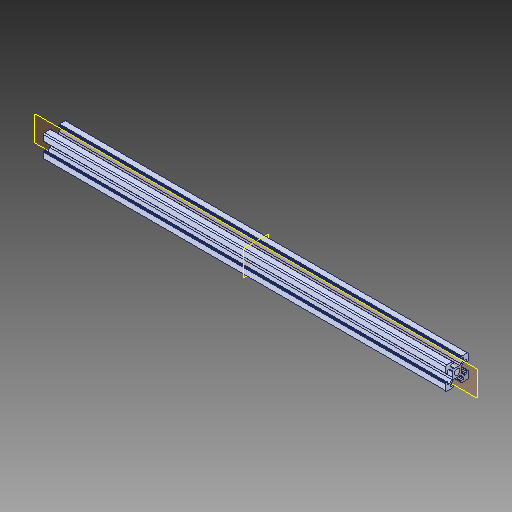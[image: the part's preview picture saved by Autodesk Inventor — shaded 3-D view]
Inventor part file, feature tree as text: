
AUTODESK INVENTOR PART (.ipt)
format: ipt  version: 2018 (Build 220112000, 112)  size: 377,344 bytes
history: native  units: in
note: dims shown in document units (in); Inventor stores cm internally (conversion verified against a paired STEP export)
features: extrude x1, plane x1, sketch x1, projected_geometry x1, fillet x1
ambient origin geometry x8: Origin, YZ Plane, XZ Plane, XY Plane, X Axis, Y Axis, Z Axis, Center Point
bodies: Solid1 (feature_tree)
feature tree (5):
  extrude  "Extrusion2"  [1 undecoded]
  plane  "Work Plane1"
  sketch  "Sketch3"  dims[d2=9.8425in d3=0.0in]
  projected_geometry  "Projected Loop2"
  fillet  "Fillet5"  [1 undecoded]
note: 2 required parameter values undecoded (feature->parameter linkage not recoverable at this tier; creation-order binding heuristic only, values carry confidence <= 0.55)
